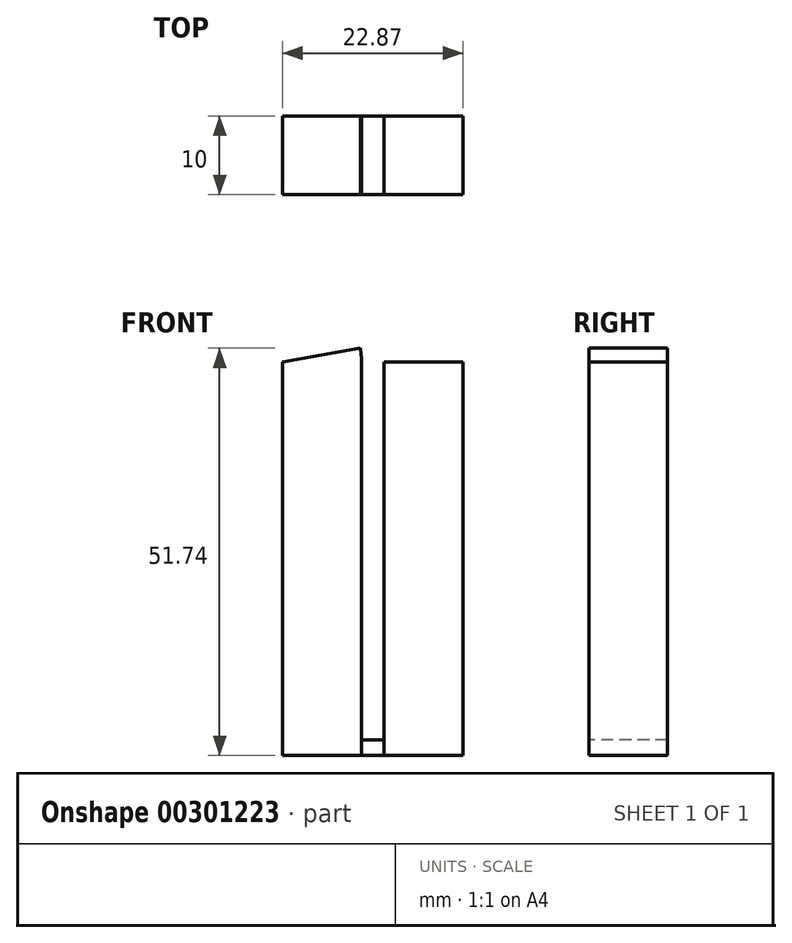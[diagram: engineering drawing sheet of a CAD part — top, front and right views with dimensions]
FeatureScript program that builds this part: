
annotation { "Feature Type Name" : "Feature", "Feature Type Description" : "" }
export const myFeature = defineFeature(function(context is Context, id is Id, definition is map)
    precondition{}
    {
        {
            var Q0;
            Q0=qCreatedBy(makeId("Top.planeOp"),FACE);
            var sketch = newSketch(context, id + "F0", { "sketchPlane" : qUnion([Q0])});
            skLineSegment(sketch, "E0.bottom", {"start": v(0, 0) * mm, "end": v(10, 0) * mm});
            skLineSegment(sketch, "E0.top", {"start": v(0, -10) * mm, "end": v(10, -10) * mm});
            skLineSegment(sketch, "E0.left", {"start": v(0, 0) * mm, "end": v(0, -10) * mm});
            skLineSegment(sketch, "E0.right", {"start": v(10, 0) * mm, "end": v(10, -10) * mm});
            skLineSegment(sketch, "E1.bottom", {"start": v(10, -10) * mm, "end": v(12.87, -10) * mm});
            skLineSegment(sketch, "E1.top", {"start": v(10, 0) * mm, "end": v(12.87, 0) * mm});
            skLineSegment(sketch, "E1.left", {"start": v(10, -10) * mm, "end": v(10, 0) * mm});
            skLineSegment(sketch, "E1.right", {"start": v(12.87, -10) * mm, "end": v(12.87, 0) * mm});
            skLineSegment(sketch, "E2.bottom", {"start": v(22.87, -10) * mm, "end": v(12.87, -10) * mm});
            skLineSegment(sketch, "E2.top", {"start": v(22.87, 0) * mm, "end": v(12.87, 0) * mm});
            skLineSegment(sketch, "E2.left", {"start": v(22.87, -10) * mm, "end": v(22.87, 0) * mm});
            skSolve(sketch);
        }
        {
            var Q0;
            Q0=makeQuery(id+"F0.imprint","IMPRINT",FACE,{"disambiguationData":[TD([[makeQuery(id+"F0.imprint","IMPRINT",EDGE,{"derivedFrom":sQuery(id+"F0.wireOp",EDGE,"E2.bottom")}),-1.0]])]});
            var Q1;
            Q1=makeQuery(id+"F0.imprint","IMPRINT",FACE,{"disambiguationData":[TD([[makeQuery(id+"F0.imprint","IMPRINT",EDGE,{"derivedFrom":sQuery(id+"F0.wireOp",EDGE,"E0.bottom")}),-1.0]])]});
            extrude(context, id + "F1", {"entities" : qUnion([Q0, Q1]), "depth" : 50 * mm});
        }
        {
            var Q0;
            Q0=makeQuery(id+"F0.imprint","IMPRINT",FACE,{"disambiguationData":[TD([[makeQuery(id+"F0.imprint","IMPRINT",EDGE,{"derivedFrom":sQuery(id+"F0.wireOp",EDGE,"E1.bottom")}),1.0]])]});
            extrude(context, id + "F2", {"entities" : qUnion([Q0]), "depth" : 2 * mm});
        }
        {
            var Q0;
            Q0=makeQuery(id+"F1.opExtrude","CAP_FACE",FACE,{"disambiguationData":[OSD([sQuery(id+"F0.wireOp",EDGE,"E0.bottom"),sQuery(id+"F0.wireOp",EDGE,"E0.top"),sQuery(id+"F0.wireOp",EDGE,"E0.left"),sQuery(id+"F0.wireOp",EDGE,"E1.left")])],"isStart":false});
            var Q1;
            Q1=makeQuery(id+"F1.opExtrude","CAP_EDGE",EDGE,{"disambiguationData":[OSD([sQuery(id+"F0.wireOp",EDGE,"E0.left")])],"isStart":false});
            revolve(context, id + "F3", {"operationType" : NewBodyOperationType.ADD, "entities" : qUnion([Q0]), "axis" : qUnion([Q1]), "revolveType" : RevolveType.ONE_DIRECTION, "angle" : 10 * degree});
        }
    });
